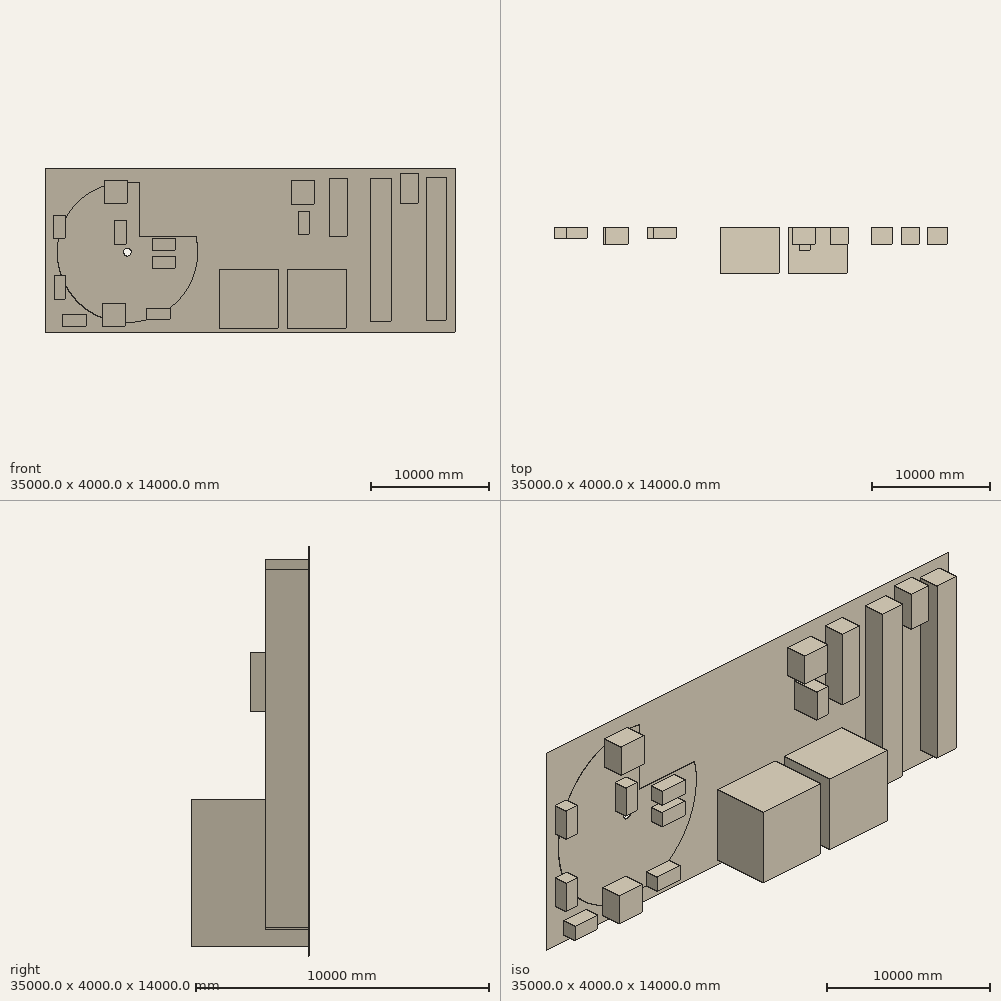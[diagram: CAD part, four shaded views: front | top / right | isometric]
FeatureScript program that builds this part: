
annotation { "Feature Type Name" : "Feature", "Feature Type Description" : "" }
export const myFeature = defineFeature(function(context is Context, id is Id, definition is map)
    precondition{}
    {
        {
            var Q0;
            Q0=qCreatedBy(makeId("Front.planeOp"),FACE);
            var sketch = newSketch(context, id + "F0", { "sketchPlane" : qUnion([Q0])});
            skLineSegment(sketch, "E0.bottom", {"start": v(-157.56, 0) * mm, "end": v(34842.44, 0) * mm});
            skLineSegment(sketch, "E0.top", {"start": v(-157.56, -14000) * mm, "end": v(34842.44, -14000) * mm});
            skLineSegment(sketch, "E0.left", {"start": v(-157.56, 0) * mm, "end": v(-157.56, -14000) * mm});
            skLineSegment(sketch, "E0.right", {"start": v(34842.44, 0) * mm, "end": v(34842.44, -14000) * mm});
            skLineSegment(sketch, "E1", {"start": v(6842.44, 0) * mm, "end": v(6842.44, -14000) * mm, "construction": true});
            skLineSegment(sketch, "E2", {"start": v(20842.44, 0) * mm, "end": v(20842.44, -14000) * mm, "construction": true});
            skLineSegment(sketch, "E3", {"start": v(13842.44, 0) * mm, "end": v(13842.44, -14000) * mm, "construction": true});
            skLineSegment(sketch, "E4", {"start": v(27842.44, 0) * mm, "end": v(27842.44, -14000) * mm, "construction": true});
            skLineSegment(sketch, "E5.bottom", {"start": v(32364.87, -775) * mm, "end": v(34042.44, -775) * mm});
            skLineSegment(sketch, "E5.top", {"start": v(32364.87, -13000) * mm, "end": v(34042.44, -13000) * mm});
            skLineSegment(sketch, "E5.left", {"start": v(32364.87, -775) * mm, "end": v(32364.87, -13000) * mm});
            skLineSegment(sketch, "E5.right", {"start": v(34042.44, -775) * mm, "end": v(34042.44, -13000) * mm});
            skLineSegment(sketch, "E6.bottom", {"start": v(27604.87, -841.44) * mm, "end": v(29364.87, -841.44) * mm});
            skLineSegment(sketch, "E6.top", {"start": v(27604.87, -13066.44) * mm, "end": v(29364.87, -13066.44) * mm});
            skLineSegment(sketch, "E6.left", {"start": v(27604.87, -841.44) * mm, "end": v(27604.87, -13066.44) * mm});
            skLineSegment(sketch, "E6.right", {"start": v(29364.87, -841.44) * mm, "end": v(29364.87, -13066.44) * mm});
            skLineSegment(sketch, "E7.bottom", {"start": v(30142.44, -454.47) * mm, "end": v(31642.44, -454.47) * mm});
            skLineSegment(sketch, "E7.top", {"start": v(30142.44, -2954.47) * mm, "end": v(31642.44, -2954.47) * mm});
            skLineSegment(sketch, "E7.left", {"start": v(30142.44, -454.47) * mm, "end": v(30142.44, -2954.47) * mm});
            skLineSegment(sketch, "E7.right", {"start": v(31642.44, -454.47) * mm, "end": v(31642.44, -2954.47) * mm});
            skLineSegment(sketch, "E8.bottom", {"start": v(25604.87, -841.44) * mm, "end": v(24104.87, -841.44) * mm});
            skLineSegment(sketch, "E8.top", {"start": v(25604.87, -5841.44) * mm, "end": v(24104.87, -5841.44) * mm});
            skLineSegment(sketch, "E8.left", {"start": v(25604.87, -841.44) * mm, "end": v(25604.87, -5841.44) * mm});
            skLineSegment(sketch, "E8.right", {"start": v(24104.87, -841.44) * mm, "end": v(24104.87, -5841.44) * mm});
            skLineSegment(sketch, "E9.bottom", {"start": v(25524.87, -13642.53) * mm, "end": v(20524.87, -13642.53) * mm});
            skLineSegment(sketch, "E9.top", {"start": v(25524.87, -8642.53) * mm, "end": v(20524.87, -8642.53) * mm});
            skLineSegment(sketch, "E9.left", {"start": v(25524.87, -13642.53) * mm, "end": v(25524.87, -8642.53) * mm});
            skLineSegment(sketch, "E9.right", {"start": v(20524.87, -13642.53) * mm, "end": v(20524.87, -8642.53) * mm});
            skLineSegment(sketch, "E10.bottom", {"start": v(19724.87, -13642.53) * mm, "end": v(14724.87, -13642.53) * mm});
            skLineSegment(sketch, "E10.top", {"start": v(19724.87, -8642.53) * mm, "end": v(14724.87, -8642.53) * mm});
            skLineSegment(sketch, "E10.left", {"start": v(19724.87, -13642.53) * mm, "end": v(19724.87, -8642.53) * mm});
            skLineSegment(sketch, "E10.right", {"start": v(14724.87, -13642.53) * mm, "end": v(14724.87, -8642.53) * mm});
            skCircle(sketch, "E11", {"center": v(6842.44, -7153.64) * mm, "radius": 323.25 * mm});
            skCircle(sketch, "E12", {"center": v(6842.44, -7153.64) * mm, "radius": 6000 * mm});
            skLineSegment(sketch, "E13.bottom", {"start": v(15060.7, 0) * mm, "end": v(19591.8, 0) * mm});
            skLineSegment(sketch, "E13.top", {"start": v(15060.7, -6739.27) * mm, "end": v(19591.8, -6739.27) * mm});
            skLineSegment(sketch, "E13.left", {"start": v(15060.7, 0) * mm, "end": v(15060.7, -6739.27) * mm});
            skLineSegment(sketch, "E13.right", {"start": v(19591.8, 0) * mm, "end": v(19591.8, -6739.27) * mm});
            skLineSegment(sketch, "E14.bottom", {"start": v(21417.66, -3636.48) * mm, "end": v(22417.66, -3636.48) * mm});
            skLineSegment(sketch, "E14.top", {"start": v(21417.66, -5636.48) * mm, "end": v(22417.66, -5636.48) * mm});
            skLineSegment(sketch, "E14.left", {"start": v(21417.66, -3636.48) * mm, "end": v(21417.66, -5636.48) * mm});
            skLineSegment(sketch, "E14.right", {"start": v(22417.66, -3636.48) * mm, "end": v(22417.66, -5636.48) * mm});
            skLineSegment(sketch, "E15.bottom", {"start": v(4842.44, -1000) * mm, "end": v(6842.44, -1000) * mm});
            skLineSegment(sketch, "E15.top", {"start": v(4842.44, -3000) * mm, "end": v(6842.44, -3000) * mm});
            skLineSegment(sketch, "E15.left", {"start": v(4842.44, -1000) * mm, "end": v(4842.44, -3000) * mm});
            skLineSegment(sketch, "E15.right", {"start": v(6842.44, -1000) * mm, "end": v(6842.44, -3000) * mm});
            skLineSegment(sketch, "E16.bottom", {"start": v(4708.36, -11500) * mm, "end": v(6708.36, -11500) * mm});
            skLineSegment(sketch, "E16.top", {"start": v(4708.36, -13500) * mm, "end": v(6708.36, -13500) * mm});
            skLineSegment(sketch, "E16.left", {"start": v(4708.36, -11500) * mm, "end": v(4708.36, -13500) * mm});
            skLineSegment(sketch, "E16.right", {"start": v(6708.36, -11500) * mm, "end": v(6708.36, -13500) * mm});
            skLineSegment(sketch, "E17.bottom", {"start": v(6767.09, -6467.58) * mm, "end": v(5767.09, -6467.58) * mm});
            skLineSegment(sketch, "E17.top", {"start": v(6767.09, -4467.58) * mm, "end": v(5767.09, -4467.58) * mm});
            skLineSegment(sketch, "E17.left", {"start": v(6767.09, -6467.58) * mm, "end": v(6767.09, -4467.58) * mm});
            skLineSegment(sketch, "E17.right", {"start": v(5767.09, -6467.58) * mm, "end": v(5767.09, -4467.58) * mm});
            skLineSegment(sketch, "E18.bottom", {"start": v(3325.92, -13500) * mm, "end": v(1325.92, -13500) * mm});
            skLineSegment(sketch, "E18.top", {"start": v(3325.92, -12500) * mm, "end": v(1325.92, -12500) * mm});
            skLineSegment(sketch, "E18.left", {"start": v(3325.92, -13500) * mm, "end": v(3325.92, -12500) * mm});
            skLineSegment(sketch, "E18.right", {"start": v(1325.92, -13500) * mm, "end": v(1325.92, -12500) * mm});
            skLineSegment(sketch, "E19.bottom", {"start": v(8478.72, -12926.21) * mm, "end": v(10478.72, -12926.21) * mm});
            skLineSegment(sketch, "E19.top", {"start": v(8478.72, -11926.21) * mm, "end": v(10478.72, -11926.21) * mm});
            skLineSegment(sketch, "E19.left", {"start": v(8478.72, -12926.21) * mm, "end": v(8478.72, -11926.21) * mm});
            skLineSegment(sketch, "E19.right", {"start": v(10478.72, -12926.21) * mm, "end": v(10478.72, -11926.21) * mm});
            skLineSegment(sketch, "E20.bottom", {"start": v(8935.46, -7519.35) * mm, "end": v(10935.46, -7519.35) * mm});
            skLineSegment(sketch, "E20.top", {"start": v(8935.46, -8519.35) * mm, "end": v(10935.46, -8519.35) * mm});
            skLineSegment(sketch, "E20.left", {"start": v(8935.46, -7519.35) * mm, "end": v(8935.46, -8519.35) * mm});
            skLineSegment(sketch, "E20.right", {"start": v(10935.46, -7519.35) * mm, "end": v(10935.46, -8519.35) * mm});
            skLineSegment(sketch, "E21.bottom", {"start": v(559.67, -4000) * mm, "end": v(1559.67, -4000) * mm});
            skLineSegment(sketch, "E21.top", {"start": v(559.67, -6000) * mm, "end": v(1559.67, -6000) * mm});
            skLineSegment(sketch, "E21.left", {"start": v(559.67, -4000) * mm, "end": v(559.67, -6000) * mm});
            skLineSegment(sketch, "E21.right", {"start": v(1559.67, -4000) * mm, "end": v(1559.67, -6000) * mm});
            skLineSegment(sketch, "E22.bottom", {"start": v(572.74, -11142.5) * mm, "end": v(1572.74, -11142.5) * mm});
            skLineSegment(sketch, "E22.top", {"start": v(572.74, -9142.5) * mm, "end": v(1572.74, -9142.5) * mm});
            skLineSegment(sketch, "E22.left", {"start": v(572.74, -11142.5) * mm, "end": v(572.74, -9142.5) * mm});
            skLineSegment(sketch, "E22.right", {"start": v(1572.74, -11142.5) * mm, "end": v(1572.74, -9142.5) * mm});
            skLineSegment(sketch, "E23.bottom", {"start": v(7871.54, -546.03) * mm, "end": v(13195.75, -546.03) * mm});
            skLineSegment(sketch, "E23.top", {"start": v(7871.54, -5818.29) * mm, "end": v(13195.75, -5818.29) * mm});
            skLineSegment(sketch, "E23.left", {"start": v(7871.54, -546.03) * mm, "end": v(7871.54, -5818.29) * mm});
            skLineSegment(sketch, "E23.right", {"start": v(13195.75, -546.03) * mm, "end": v(13195.75, -5818.29) * mm});
            skPoint(sketch, "E24.oppositeSnap0", {"position": v(20842.44, -7000) * mm});
            skLineSegment(sketch, "E24.bottom", {"start": v(8936.38, -6000) * mm, "end": v(10936.38, -6000) * mm});
            skLineSegment(sketch, "E24.top", {"start": v(8936.38, -7000) * mm, "end": v(10936.38, -7000) * mm});
            skLineSegment(sketch, "E24.left", {"start": v(8936.38, -6000) * mm, "end": v(8936.38, -7000) * mm});
            skLineSegment(sketch, "E24.right", {"start": v(10936.38, -6000) * mm, "end": v(10936.38, -7000) * mm});
            skLineSegment(sketch, "E25.bottom", {"start": v(20842.44, -1039.31) * mm, "end": v(22842.44, -1039.31) * mm});
            skLineSegment(sketch, "E25.top", {"start": v(20842.44, -3039.31) * mm, "end": v(22842.44, -3039.31) * mm});
            skLineSegment(sketch, "E25.left", {"start": v(20842.44, -1039.31) * mm, "end": v(20842.44, -3039.31) * mm});
            skLineSegment(sketch, "E25.right", {"start": v(22842.44, -1039.31) * mm, "end": v(22842.44, -3039.31) * mm});
            skSolve(sketch);
        }
        {
            var Q0;
            Q0=makeQuery(id+"F0.imprint","IMPRINT",FACE,{"disambiguationData":[TD([[makeQuery(id+"F0.imprint","IMPRINT",EDGE,{"derivedFrom":sQuery(id+"F0.wireOp",EDGE,"E5.bottom")}),-1.0]])]});
            var Q1;
            Q1=makeQuery(id+"F0.imprint","IMPRINT",FACE,{"disambiguationData":[TD([[makeQuery(id+"F0.imprint","IMPRINT",EDGE,{"derivedFrom":sQuery(id+"F0.wireOp",EDGE,"E6.bottom")}),-1.0]])]});
            var Q2;
            Q2=makeQuery(id+"F0.imprint","IMPRINT",FACE,{"disambiguationData":[TD([[makeQuery(id+"F0.imprint","IMPRINT",EDGE,{"derivedFrom":sQuery(id+"F0.wireOp",EDGE,"E8.bottom")}),1.0]])]});
            var Q3;
            Q3=makeQuery(id+"F0.imprint","IMPRINT",FACE,{"disambiguationData":[TD([[makeQuery(id+"F0.imprint","IMPRINT",EDGE,{"derivedFrom":sQuery(id+"F0.wireOp",EDGE,"E7.bottom")}),-1.0]])]});
            extrude(context, id + "F1", {"entities" : qUnion([Q0, Q1, Q2, Q3]), "depth" : 1500 * mm});
        }
        {
            var Q0;
            Q0 = qSketchRegion(id + "F0", true);
            var Q1;
            {var subQ0=sQuery(id+"F0.wireOp",EDGE,"E23.left");var subQ1=sQuery(id+"F0.wireOp",EDGE,"E12");var subQ2=makeQuery(id+"F0.imprint","INTERSECT",VERTEX,{"derivedFrom":[subQ1,subQ0]});Q1=makeQuery(id+"F0.imprint","IMPRINT",FACE,{"disambiguationData":[TD([[makeQuery(id+"F0.imprint","IMPRINT",EDGE,{"disambiguationData":[TD([[subQ2,1.0]])],"derivedFrom":subQ1}),1.0]])]});}
            var Q2;
            {var subQ1=sQuery(id+"F0.wireOp",EDGE,"E23.bottom");Q2=makeQuery(id+"F0.imprint","IMPRINT",FACE,{"disambiguationData":[TD([[makeQuery(id+"F0.imprint","IMPRINT",EDGE,{"derivedFrom":subQ1}),-1.0]])]});}
            extrude(context, id + "F2", {"entities" : qUnion([Q0, Q1, Q2]), "depth" : 25 * mm});
        }
        {
            var Q0;
            Q0=makeQuery(id+"F0.imprint","IMPRINT",FACE,{"disambiguationData":[TD([[makeQuery(id+"F0.imprint","IMPRINT",EDGE,{"derivedFrom":sQuery(id+"F0.wireOp",EDGE,"E10.bottom")}),-1.0]])]});
            var Q1;
            Q1=makeQuery(id+"F0.imprint","IMPRINT",FACE,{"disambiguationData":[TD([[makeQuery(id+"F0.imprint","IMPRINT",EDGE,{"derivedFrom":sQuery(id+"F0.wireOp",EDGE,"E9.bottom")}),-1.0]])]});
            extrude(context, id + "F3", {"entities" : qUnion([Q0, Q1]), "operationType" : NewBodyOperationType.ADD, "depth" : 4000 * mm});
        }
        {
            var Q0;
            Q0=makeQuery(id+"F0.imprint","IMPRINT",FACE,{"disambiguationData":[TD([[makeQuery(id+"F0.imprint","IMPRINT",EDGE,{"derivedFrom":sQuery(id+"F0.wireOp",EDGE,"phswzlI5-mL31-dBBv-ndzZ-SrZosMlNJSPl.bottom")}),1.0]])]});
            var Q1;
            {var subQ5=sQuery(id+"F0.wireOp",EDGE,"E15.top");Q1=makeQuery(id+"F0.imprint","IMPRINT",FACE,{"disambiguationData":[TD([[makeQuery(id+"F0.imprint","IMPRINT",EDGE,{"derivedFrom":subQ5}),1.0]])]});}
            var Q2;
            {var subQ5=sQuery(id+"F0.wireOp",EDGE,"E15.bottom");Q2=makeQuery(id+"F0.imprint","IMPRINT",FACE,{"disambiguationData":[TD([[makeQuery(id+"F0.imprint","IMPRINT",EDGE,{"derivedFrom":subQ5}),-1.0]])]});}
            var Q3;
            {var subQ5=sQuery(id+"F0.wireOp",EDGE,"E16.bottom");Q3=makeQuery(id+"F0.imprint","IMPRINT",FACE,{"disambiguationData":[TD([[makeQuery(id+"F0.imprint","IMPRINT",EDGE,{"derivedFrom":subQ5}),-1.0]])]});}
            var Q4;
            {var subQ5=sQuery(id+"F0.wireOp",EDGE,"E16.top");Q4=makeQuery(id+"F0.imprint","IMPRINT",FACE,{"disambiguationData":[TD([[makeQuery(id+"F0.imprint","IMPRINT",EDGE,{"derivedFrom":subQ5}),1.0]])]});}
            var Q5;
            Q5=makeQuery(id+"F0.imprint","IMPRINT",FACE,{"disambiguationData":[TD([[makeQuery(id+"F0.imprint","IMPRINT",EDGE,{"derivedFrom":sQuery(id+"F0.wireOp",EDGE,"E25.bottom")}),-1.0]])]});
            extrude(context, id + "F4", {"entities" : qUnion([Q0, Q1, Q2, Q3, Q4, Q5]), "operationType" : NewBodyOperationType.ADD, "depth" : 1500 * mm});
        }
        {
            var Q0;
            Q0=makeQuery(id+"F0.imprint","IMPRINT",FACE,{"disambiguationData":[TD([[makeQuery(id+"F0.imprint","IMPRINT",EDGE,{"derivedFrom":sQuery(id+"F0.wireOp",EDGE,"E11")}),-1.0]])]});
            extrude(context, id + "F5", {"entities" : qUnion([Q0]), "operationType" : NewBodyOperationType.ADD, "depth" : 50 * mm});
        }
        {
            var Q0;
            Q0=makeQuery(id+"F0.imprint","IMPRINT",FACE,{"disambiguationData":[TD([[makeQuery(id+"F0.imprint","IMPRINT",EDGE,{"derivedFrom":sQuery(id+"F0.wireOp",EDGE,"E14.bottom")}),-1.0]])]});
            extrude(context, id + "F6", {"entities" : qUnion([Q0]), "operationType" : NewBodyOperationType.ADD, "depth" : 2000 * mm});
        }
        {
            var Q0;
            {var subQ0=sQuery(id+"F0.wireOp",EDGE,"PWz8wkNr-aK8F-07dL-arwI-qm2rY6ms5QoO.top");var subQ1=sQuery(id+"F0.wireOp",EDGE,"E12");var subQ2=makeQuery(id+"F0.imprint","INTERSECT",VERTEX,{"derivedFrom":[subQ1,subQ0]});Q0=makeQuery(id+"F0.imprint","IMPRINT",FACE,{"disambiguationData":[TD([[makeQuery(id+"F0.imprint","IMPRINT",EDGE,{"disambiguationData":[TD([[subQ2,-1.0]])],"derivedFrom":subQ1}),1.0]])]});}
            var Q1;
            {var subQ1=sQuery(id+"F0.wireOp",EDGE,"PWz8wkNr-aK8F-07dL-arwI-qm2rY6ms5QoO.bottom");Q1=makeQuery(id+"F0.imprint","IMPRINT",FACE,{"disambiguationData":[TD([[makeQuery(id+"F0.imprint","IMPRINT",EDGE,{"derivedFrom":subQ1}),-1.0]])]});}
            extrude(context, id + "F7", {"entities" : qUnion([Q0, Q1]), "operationType" : NewBodyOperationType.ADD, "depth" : 25 * mm});
        }
        {
            var Q0;
            Q0=makeQuery(id+"F0.imprint","IMPRINT",FACE,{"disambiguationData":[TD([[makeQuery(id+"F0.imprint","IMPRINT",EDGE,{"derivedFrom":sQuery(id+"F0.wireOp",EDGE,"E17.bottom")}),-1.0]])]});
            var Q1;
            {var subQ4=sQuery(id+"F0.wireOp",EDGE,"E21.bottom");Q1=makeQuery(id+"F0.imprint","IMPRINT",FACE,{"disambiguationData":[TD([[makeQuery(id+"F0.imprint","IMPRINT",EDGE,{"derivedFrom":subQ4}),-1.0]])]});}
            var Q2;
            {var subQ0=sQuery(id+"F0.wireOp",EDGE,"E21.right");var subQ1=sQuery(id+"F0.wireOp",EDGE,"E12");var subQ2=makeQuery(id+"F0.imprint","INTERSECT",VERTEX,{"derivedFrom":[subQ1,subQ0]});Q2=makeQuery(id+"F0.imprint","IMPRINT",FACE,{"disambiguationData":[TD([[makeQuery(id+"F0.imprint","IMPRINT",EDGE,{"disambiguationData":[TD([[subQ2,-1.0]])],"derivedFrom":subQ1}),1.0]])]});}
            var Q3;
            {var subQ4=sQuery(id+"F0.wireOp",EDGE,"E22.bottom");Q3=makeQuery(id+"F0.imprint","IMPRINT",FACE,{"disambiguationData":[TD([[makeQuery(id+"F0.imprint","IMPRINT",EDGE,{"derivedFrom":subQ4}),1.0]])]});}
            var Q4;
            {var subQ0=sQuery(id+"F0.wireOp",EDGE,"E22.top");var subQ1=sQuery(id+"F0.wireOp",EDGE,"E12");var subQ2=makeQuery(id+"F0.imprint","INTERSECT",VERTEX,{"derivedFrom":[subQ1,subQ0]});Q4=makeQuery(id+"F0.imprint","IMPRINT",FACE,{"disambiguationData":[TD([[makeQuery(id+"F0.imprint","IMPRINT",EDGE,{"disambiguationData":[TD([[subQ2,-1.0]])],"derivedFrom":subQ1}),1.0]])]});}
            var Q5;
            Q5=makeQuery(id+"F0.imprint","IMPRINT",FACE,{"disambiguationData":[TD([[makeQuery(id+"F0.imprint","IMPRINT",EDGE,{"derivedFrom":sQuery(id+"F0.wireOp",EDGE,"E18.bottom")}),-1.0]])]});
            var Q6;
            {var subQ2=sQuery(id+"F0.wireOp",EDGE,"E19.top");Q6=makeQuery(id+"F0.imprint","IMPRINT",FACE,{"disambiguationData":[TD([[makeQuery(id+"F0.imprint","IMPRINT",EDGE,{"derivedFrom":subQ2}),-1.0]])]});}
            var Q7;
            {var subQ0=sQuery(id+"F0.wireOp",EDGE,"E19.bottom");Q7=makeQuery(id+"F0.imprint","IMPRINT",FACE,{"disambiguationData":[TD([[makeQuery(id+"F0.imprint","IMPRINT",EDGE,{"derivedFrom":subQ0}),1.0]])]});}
            var Q8;
            Q8=makeQuery(id+"F0.imprint","IMPRINT",FACE,{"disambiguationData":[TD([[makeQuery(id+"F0.imprint","IMPRINT",EDGE,{"derivedFrom":sQuery(id+"F0.wireOp",EDGE,"E20.bottom")}),-1.0]])]});
            var Q9;
            Q9=makeQuery(id+"F0.imprint","IMPRINT",FACE,{"disambiguationData":[TD([[makeQuery(id+"F0.imprint","IMPRINT",EDGE,{"derivedFrom":sQuery(id+"F0.wireOp",EDGE,"E24.bottom")}),-1.0]])]});
            extrude(context, id + "F8", {"entities" : qUnion([Q0, Q1, Q2, Q3, Q4, Q5, Q6, Q7, Q8, Q9]), "operationType" : NewBodyOperationType.ADD, "depth" : 1000 * mm});
        }
    });
